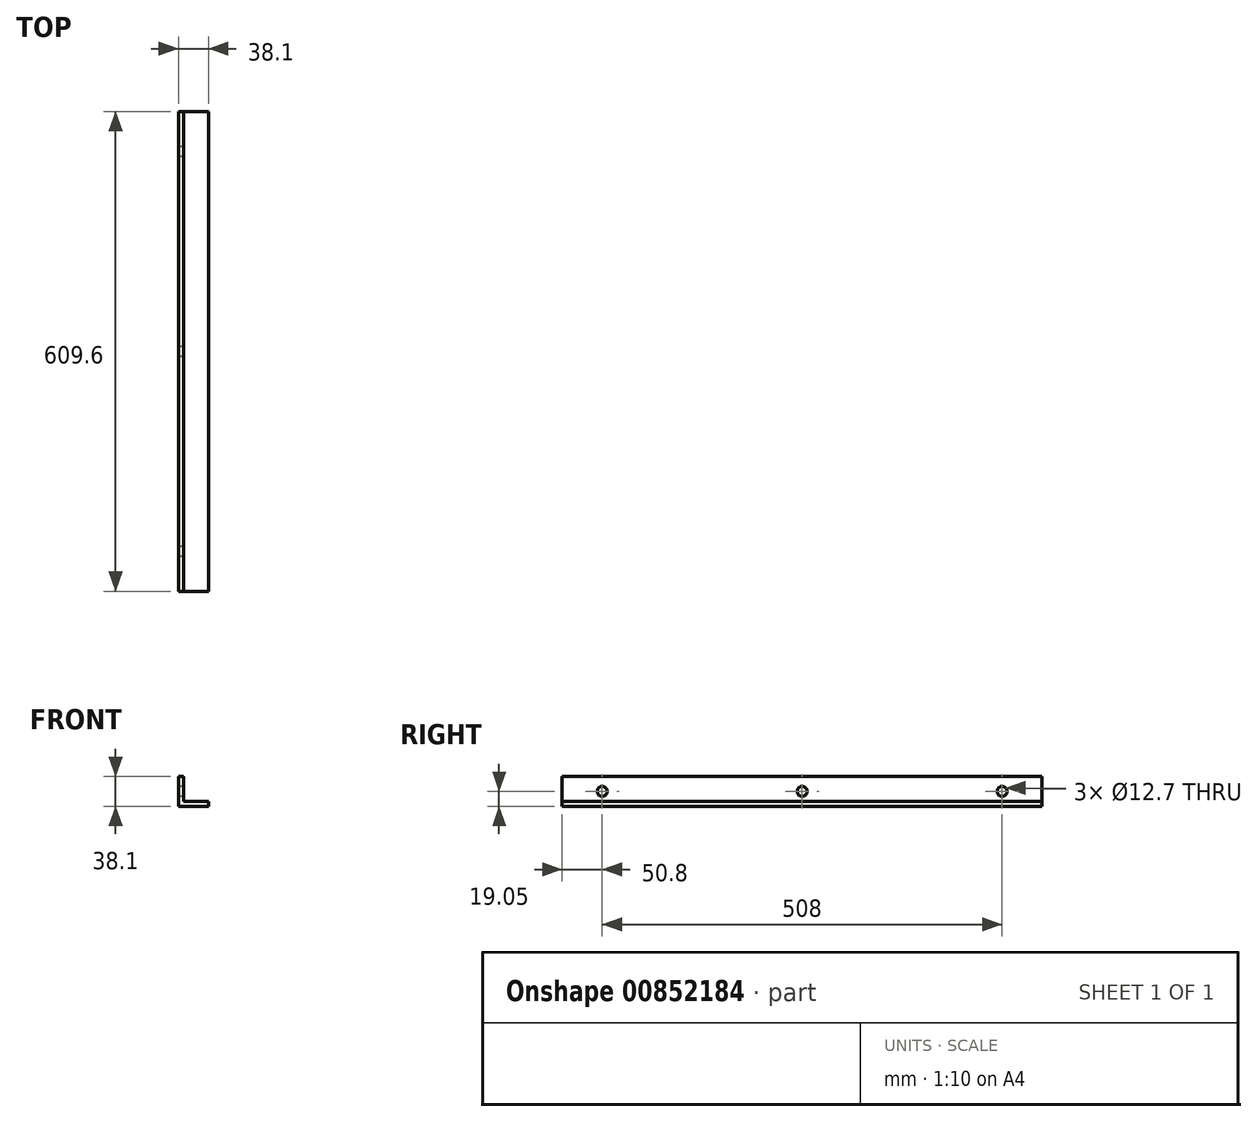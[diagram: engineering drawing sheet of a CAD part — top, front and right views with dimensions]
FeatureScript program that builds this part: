
annotation { "Feature Type Name" : "Feature", "Feature Type Description" : "" }
export const myFeature = defineFeature(function(context is Context, id is Id, definition is map)
    precondition{}
    {
        {
            var Q0;
            Q0=qCreatedBy(makeId("Front.planeOp"),FACE);
            var sketch = newSketch(context, id + "F0", { "sketchPlane" : qUnion([Q0])});
            skLineSegment(sketch, "E0", {"start": v(0, 0) * mm, "end": v(0, 38.1) * mm});
            skLineSegment(sketch, "E1", {"start": v(0, 38.1) * mm, "end": v(6.35, 38.1) * mm});
            skLineSegment(sketch, "E2", {"start": v(6.35, 38.1) * mm, "end": v(6.35, 6.35) * mm});
            skLineSegment(sketch, "E3", {"start": v(6.35, 6.35) * mm, "end": v(38.1, 6.35) * mm});
            skLineSegment(sketch, "E4", {"start": v(38.1, 6.35) * mm, "end": v(38.1, 0) * mm});
            skLineSegment(sketch, "E5", {"start": v(38.1, 0) * mm, "end": v(0, 0) * mm});
            skSolve(sketch);
        }
        {
            var Q0;
            Q0 = qSketchRegion(id + "F0", true);
            extrude(context, id + "F1", {"entities" : qUnion([Q0]), "depth" : 609.6 * mm, "offsetDistance" : 25.4 * mm});
        }
        {
            var Q0;
            Q0=qCreatedBy(makeId("Right.planeOp"),FACE);
            var sketch = newSketch(context, id + "F2", { "sketchPlane" : qUnion([Q0])});
            skLineSegment(sketch, "E6", {"start": v(-606.52, 19.05) * mm, "end": v(-5.82, 19.05) * mm, "construction": true});
            skCircle(sketch, "E7", {"center": v(-50.8, 19.05) * mm, "radius": 6.35 * mm});
            skCircle(sketch, "E8", {"center": v(-304.8, 19.05) * mm, "radius": 6.35 * mm});
            skCircle(sketch, "E9", {"center": v(-558.8, 19.05) * mm, "radius": 6.35 * mm});
            skSolve(sketch);
        }
        {
            var Q0;
            Q0 = qSketchRegion(id + "F2", true);
            extrude(context, id + "F3", {"entities" : qUnion([Q0]), "operationType" : NewBodyOperationType.REMOVE, "depth" : 25.4 * mm, "offsetDistance" : 25.4 * mm});
        }
    });
